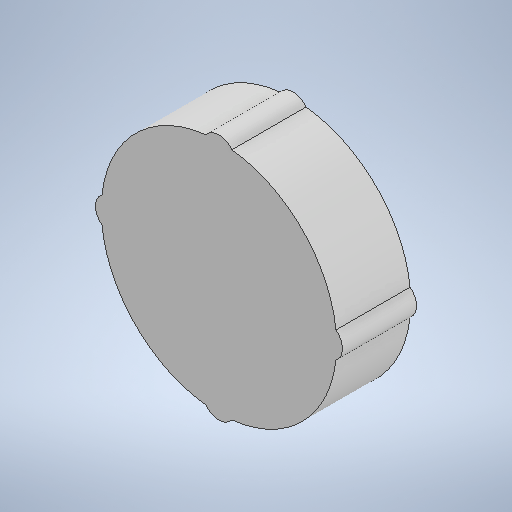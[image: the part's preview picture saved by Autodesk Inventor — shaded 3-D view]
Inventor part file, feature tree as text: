
AUTODESK INVENTOR PART (.ipt)
format: ipt  version: 2025.1 (Build 291241000, 241)  size: 249,856 bytes
history: native  units: mm
features: sketch x2, extrude x1
ambient origin geometry x8: Origin, YZ Plane, XZ Plane, XY Plane, X Axis, Y Axis, Z Axis, Center Point
bodies: Solid1 (feature_tree)
feature tree (3):
  extrude  "Extrusion1"  Depth=10.0mm
  sketch  "Sketch1"  dims[d0=10.0mm d1=0.25mm]
  sketch  "Skizze - Runde Anordnung1"  dims[d2=40.0mm d4=360.0deg d6=70.05mm d7=0.25mm d8=74.060786mm d9=73.5mm d10=21.9mm d11=0.0mm]
